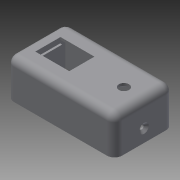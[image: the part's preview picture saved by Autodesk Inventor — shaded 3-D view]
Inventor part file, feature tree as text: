
AUTODESK INVENTOR PART (.ipt)
format: ipt  version: 2014 (Build 180170000, 170)  size: 193,536 bytes
history: native  units: mm
features: sketch x8, extrude x7, chamfer x3, fillet x2, projected_geometry x1
ambient origin geometry x8: Origin, YZ Plane, XZ Plane, XY Plane, X Axis, Y Axis, Z Axis, Center Point
bodies: Solid1 (feature_tree)
feature tree (21):
  extrude  "Extrusion1"  Depth=41.0mm
  extrude  "Extrusion2"  Depth=47.0mm
  sketch  "Sketch4"  dims[d4=30.0mm d5=0.0mm d6=3.0mm d7=0.0mm]
  extrude  "Extrusion3"  Depth=3.0mm TaperAngle=0.0deg
  extrude  "Extrusion4"  Depth=40.0mm
  chamfer  "Chamfer1"  Distance=3.0mm
  chamfer  "Chamfer2"  Distance=8.0mm
  fillet  "Fillet1"  Radius=20.5mm
  fillet  "Fillet2"  Radius=13.0mm
  extrude  "Extrusion5"  Depth=3.0mm TaperAngle=0.0deg
  chamfer  "Chamfer3"  Distance=1.0mm Angle=45.0deg
  extrude  "Extrusion6"  Depth=1.6mm TaperAngle=45.0deg
  extrude  "Extrusion7"  Depth=6.0mm
  sketch  "Sketch1"  dims[d0=80.0mm d1=41.0mm]
  sketch  "Sketch2"  dims[d2=86.0mm d3=47.0mm]
  sketch  "Sketch5"  dims[d12=79.0mm d13=40.0mm]
  sketch  "Sketch6"  dims[d14=27.0mm]
  sketch  "Sketch7"  dims[d15=20.0mm]
  sketch  "Sketch8"  dims[d16=10.25mm]
  sketch  "Sketch9"  dims[d17=6.27mm d18=3.0mm d19=0.0mm d20=8.0mm d21=20.5mm d22=13.0mm d23=3.0mm d24=0.0mm d25=1.0mm d26=2.0mm d27=45.0deg d28=1.0mm d29=2.0mm d30=45.0deg d31=6.0mm d32=6.0mm d33=3.5mm d34=10.0mm d35=10.0mm d36=0.0mm d37=2.0mm d38=2.0mm d39=45.0deg d40=3.0mm d41=32.0mm d42=8.0mm d43=1.6mm d44=0.0mm d45=1.6mm d46=0.0mm]
  projected_geometry  "Projected Loop2"
